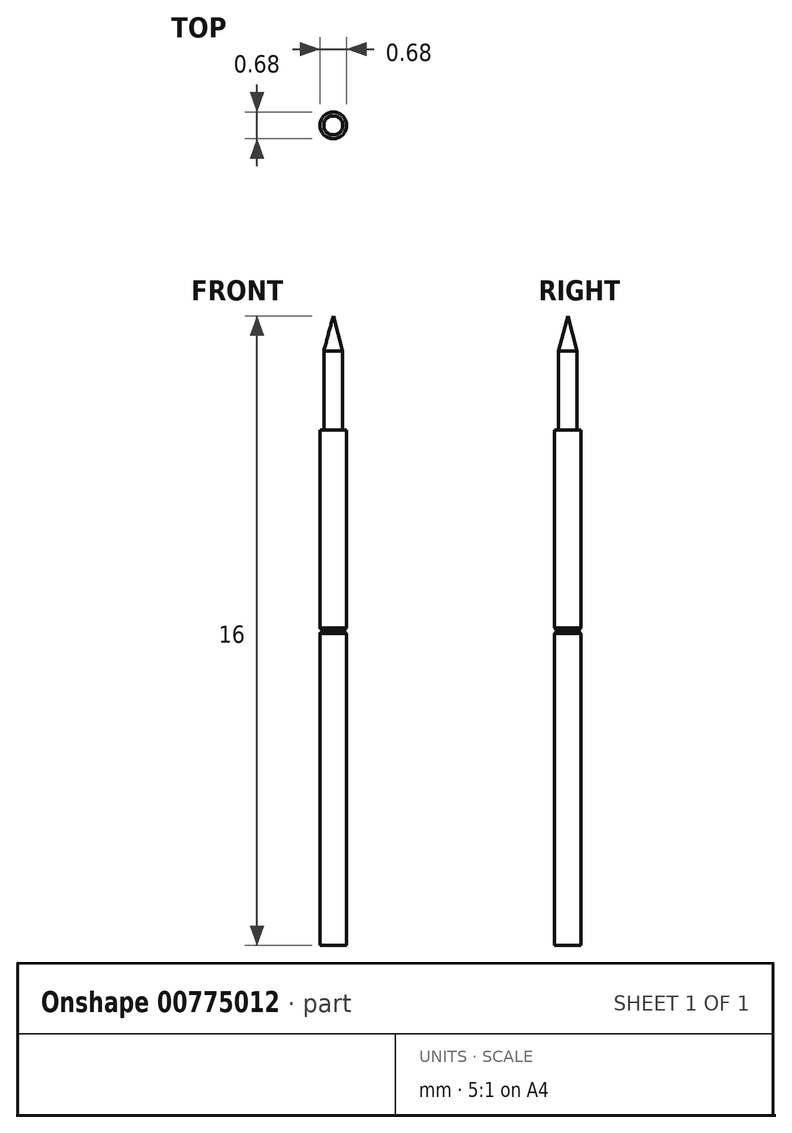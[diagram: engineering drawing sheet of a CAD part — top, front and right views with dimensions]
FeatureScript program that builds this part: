
annotation { "Feature Type Name" : "Feature", "Feature Type Description" : "" }
export const myFeature = defineFeature(function(context is Context, id is Id, definition is map)
    precondition{}
    {
        {
            var Q0;
            Q0=qCreatedBy(makeId("Front.planeOp"),FACE);
            var sketch = newSketch(context, id + "F0", { "sketchPlane" : qUnion([Q0])});
            skLineSegment(sketch, "E0", {"start": v(0, 0) * mm, "end": v(0.24, -0.9) * mm});
            skLineSegment(sketch, "E1", {"start": v(0.24, -2.9) * mm, "end": v(0.34, -2.9) * mm});
            skLineSegment(sketch, "E2", {"start": v(0.34, -2.9) * mm, "end": v(0.34, -7.93) * mm});
            skLineSegment(sketch, "E3", {"start": v(0.34, -7.93) * mm, "end": v(0.27, -8) * mm});
            skLineSegment(sketch, "E4", {"start": v(0.27, -8) * mm, "end": v(0.34, -8.07) * mm});
            skLineSegment(sketch, "E5", {"start": v(0.34, -8.07) * mm, "end": v(0.34, -16) * mm});
            skLineSegment(sketch, "E6", {"start": v(0.34, -16) * mm, "end": v(0, -16) * mm});
            skLineSegment(sketch, "E7", {"start": v(0, -16) * mm, "end": v(0, 0) * mm});
            skLineSegment(sketch, "E8", {"start": v(0.24, -0.9) * mm, "end": v(0.24, -2.9) * mm});
            skSolve(sketch);
        }
        {
            var Q0;
            Q0 = qSketchRegion(id + "F0", true);
            var Q1;
            Q1=sQuery(id+"F0.wireOp",EDGE,"E7");
            revolve(context, id + "F1", {"surfaceOperationType" : NewSurfaceOperationType.NEW, "entities" : qUnion([Q0]), "axis" : qUnion([Q1]), "revolveType" : RevolveType.FULL});
        }
    });
